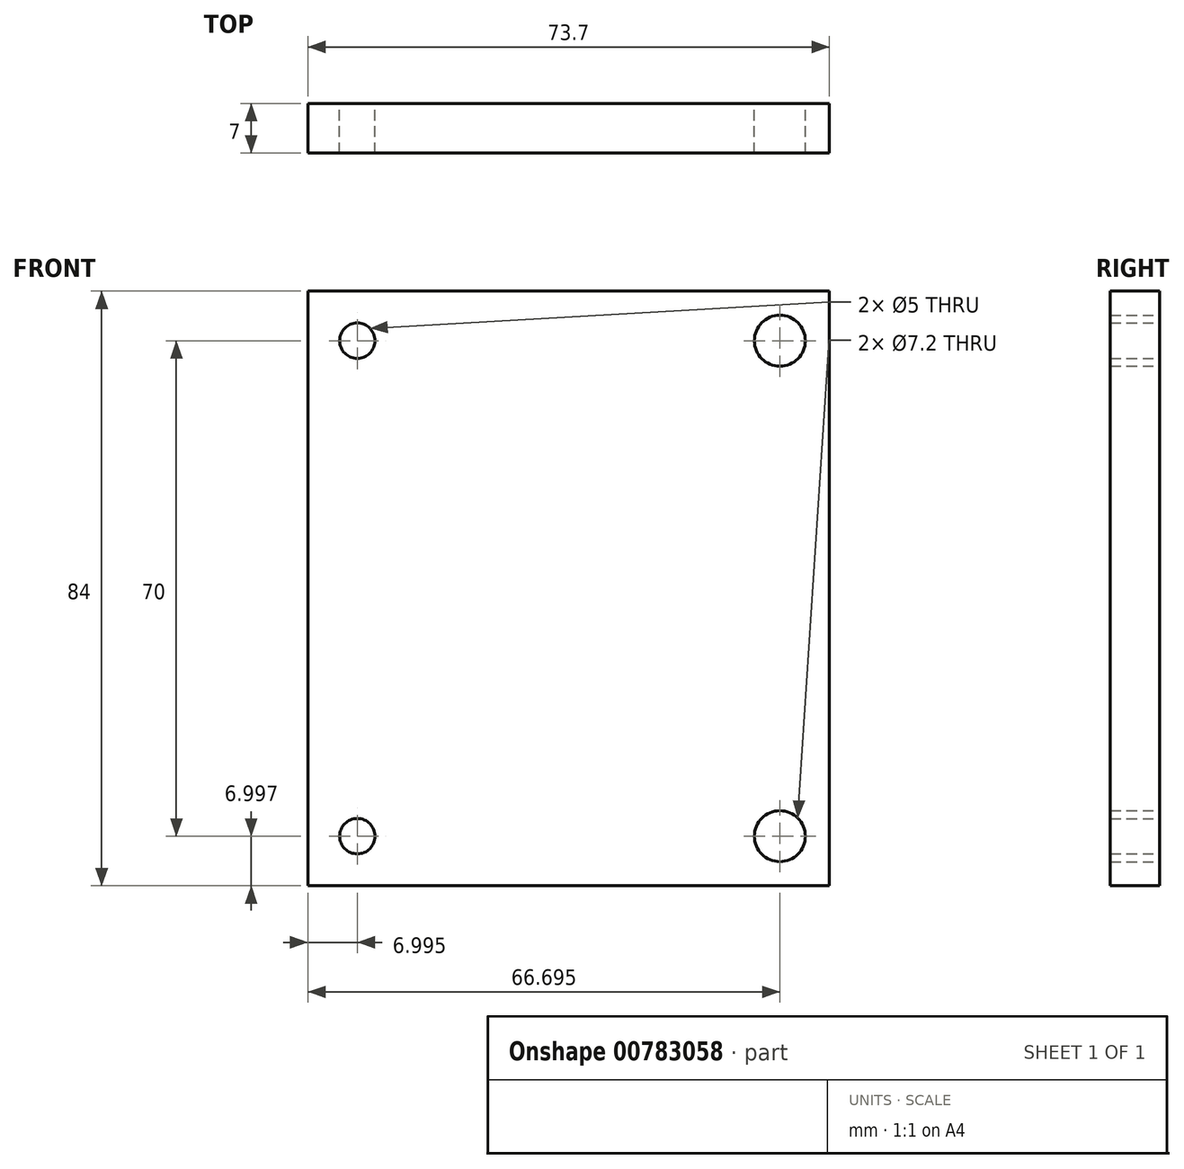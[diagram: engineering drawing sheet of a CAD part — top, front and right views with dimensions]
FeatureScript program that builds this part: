
annotation { "Feature Type Name" : "Feature", "Feature Type Description" : "" }
export const myFeature = defineFeature(function(context is Context, id is Id, definition is map)
    precondition{}
    {
        {
            var Q0;
            Q0=qCreatedBy(makeId("Front.planeOp"),FACE);
            var sketch = newSketch(context, id + "F0", { "sketchPlane" : qUnion([Q0])});
            skLineSegment(sketch, "E0.bottom", {"start": v(-68.94, 63.54) * mm, "end": v(4.76, 63.54) * mm});
            skLineSegment(sketch, "E0.top", {"start": v(-68.94, -20.46) * mm, "end": v(4.76, -20.46) * mm});
            skLineSegment(sketch, "E0.left", {"start": v(-68.94, 63.54) * mm, "end": v(-68.94, -20.46) * mm});
            skLineSegment(sketch, "E0.right", {"start": v(4.76, 63.54) * mm, "end": v(4.76, -20.46) * mm});
            skCircle(sketch, "E1", {"center": v(-61.94, -13.46) * mm, "radius": 2.5 * mm});
            skCircle(sketch, "E2", {"center": v(-2.24, -13.46) * mm, "radius": 3.6 * mm});
            skCircle(sketch, "E3.0.1.0", {"center": v(-61.94, 56.54) * mm, "radius": 2.5 * mm});
            skCircle(sketch, "E3.0.1.1", {"center": v(-2.24, 56.54) * mm, "radius": 3.6 * mm});
            skLineSegment(sketch, "E3.direction1", {"start": v(-61.94, -13.46) * mm, "end": v(-36.94, -13.46) * mm, "construction": true});
            skLineSegment(sketch, "E3.direction2", {"start": v(-61.94, -13.46) * mm, "end": v(-61.94, 56.54) * mm, "construction": true});
            skSolve(sketch);
        }
        {
            var Q0;
            Q0=makeQuery(id+"F0.imprint","IMPRINT",FACE,{"disambiguationData":[TD([[makeQuery(id+"F0.imprint","IMPRINT",EDGE,{"derivedFrom":sQuery(id+"F0.wireOp",EDGE,"E0.bottom")}),-1.0]])]});
            extrude(context, id + "F1", {"entities" : qUnion([Q0]), "depth" : 7 * mm, "offsetDistance" : 25 * mm});
        }
    });
